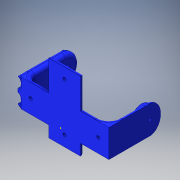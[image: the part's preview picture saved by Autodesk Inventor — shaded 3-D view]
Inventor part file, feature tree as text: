
AUTODESK INVENTOR PART (.ipt)
format: ipt  version: 2016 (Build 200138000, 138)  size: 574,464 bytes
history: native  units: in
note: dims shown in document units (in); Inventor stores cm internally (conversion verified against a paired STEP export)
features: sketch x13, other x3
ambient origin geometry x8: Origin, YZ Plane, XZ Plane, XY Plane, X Axis, Y Axis, Z Axis, Center Point
bodies: Solid1 (feature_tree)
feature tree (16):
  other  "Kne_v2.ipt"
  other  "Solid1::Kne_v2.ipt"
  other  "TaggingFeature1"
  sketch  "Sketch1"  dims[d0=0.3937in]
  sketch  "Sketch4"
  sketch  "Sketch5"
  sketch  "Sketch7"
  sketch  "Sketch9"
  sketch  "Sketch10"
  sketch  "Sketch15"
  sketch  "Sketch16"
  sketch  "Sketch17"
  sketch  "Sketch18"
  sketch  "Sketch19"
  sketch  "Sketch20"
  sketch  "Sketch21"
